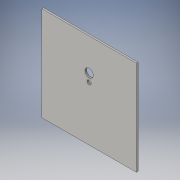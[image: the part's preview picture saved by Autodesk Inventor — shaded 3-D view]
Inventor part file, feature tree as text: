
AUTODESK INVENTOR PART (.ipt)
format: ipt  version: 2016 (Build 200138000, 138)  size: 111,616 bytes
history: native  units: in
note: dims shown in document units (in); Inventor stores cm internally (conversion verified against a paired STEP export)
features: extrude x3, sketch x3, projected_geometry x2
ambient origin geometry x8: Origin, YZ Plane, XZ Plane, XY Plane, X Axis, Y Axis, Z Axis, Center Point
bodies: Solid1 (feature_tree)
feature tree (8):
  extrude  "Extrusion1"  Depth=7.0in
  extrude  "Extrusion2"  Depth=0.125in
  extrude  "Extrusion3"  Depth=2.0in
  sketch  "Sketch1"  dims[d0=7.0in d1=7.0in]
  sketch  "Sketch2"  dims[d2=0.125in d3=0.0in d4=0.5in]
  projected_geometry  "Projected Loop1"
  sketch  "Sketch3"  dims[d5=0.5in d6=2.0in d7=0.75in d8=0.62in d9=1.0in d10=0.0in d11=0.8in d12=0.2in d13=0.308in d14=1.0in d15=0.0in]
  projected_geometry  "Projected Loop2"
